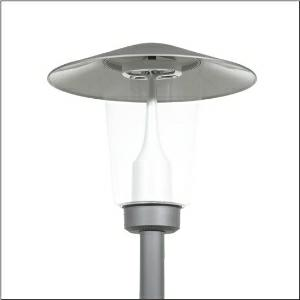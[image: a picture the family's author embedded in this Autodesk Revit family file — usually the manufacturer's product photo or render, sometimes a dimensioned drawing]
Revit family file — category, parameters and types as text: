
# Revit family: pilzleuchte_iq___st1_2a_5xa5235af14h_f6cb
name_source: partatom
category: Lighting Fixtures
units: mm (PartAtom-declared; Revit-internal decimal feet)

## family parameters
Cut with Voids When Loaded = No
Host = Face
Light Source = No
Part Type = Normal
Room Calculation Point = No
Round Connector Dimension = Use Diameter
Shared = No

## types (1)
- --- (1 x LED, 1550 lm, 12.9 W, 2200K)
    Apparent Load = 13 VA
    CIE Flux Codes = 24 61 93 98 100
    Color Rendering = 70
    Color Temperature = 2200K
    Default Elevation = 1800 mm
    Description = Mushroom Luminaire iQ, mast luminaire, Module 540 iQ-SR, primary light control with 3 zone facetted reflector, of plastic, silver coated, highly specular, structured, primary optical cover: cover, of PMMA, transparent, light distribution: ST1.2a, light emission: direct distribution, primary light characteristic: asymmetric, installation type: post-top, LED, High Power LED, rated luminous flux: 1.550lm, luminous efficacy: 120lm/W, light colour: 722, colour temperature: 2200K, control gear: iQ Street-Remote, control: pre-setting: logarithmic dimming characteristic, Street-Remote, Auto-Match, Temp-Guard, Lumen-Switch, Night-Set, Smart-Wire, Light-Fading, Desk-Remote (wireless, voltage-free reading and setting of iQ features in the workshop via application-optimized NFC function/RFID function), optimised constant luminous flux control (CLO 2.0), with terminal, 6-pole, max. 2.5mm², mains connection: 230..240V, AC, 50/60Hz, start of lifetime: 13W, end of service life: 13W, reduction: 6W, luminaire housing, upper part, of glass-fibre reinforced polyester, coated, Siteco® metallic grey (DB 702S), diameter: 650mm, height: 586mm, spigot size: d x l = 76 x 70mm (post-top) | with reducer (optional accessory) 60 x 70mm, mounting height: 3..5m, post-top mast mounting element, of diecast aluminium, coated, Siteco® metallic grey (DB 702S), Module 540 iQ-SR, traffic white (RAL 9016), equipment: standard, protection rating (complete): IP65, insulation class (complete): insulation class II (safety insulation), certification: CE, ENEC, VDE, packaging unit: 1 piece

Light Distribution: ST1.2a
    Height = 586 mm
    Lamp = 1 x LED
    Lamp Light Flux = 1550 lm
    Lamp Power = 12.9 W
    Lamp count = 1
    Length = 650 mm
    Luminous efficacy = 120 lm/W
    Manufacturer = Siteco
    ModVariant = No
    Model = 5XA5235AF14H
    Number of Poles = 1
    OnlyDefault = Yes
    Power Factor = 1
    Product Name = Pilzleuchte iQ | ST1.2a
    Product group = mast luminaire | pylon top
    ProductGroupID = 6100
    Protection Class = Protection class II
    Protection Degree = IP 65
    RLX_Detail_Level = 1
    RLX_Emergency_Light_Flux = 0 lm
    RLX_Emergency_Type = 0
    RLX_Emergency_Type_DB = No
    RlxData = <blob elided: 124257 chars, md5=b4fa3d6c>
    Socket = socket
    Standby Power = 0 W
    System Light Flux = 1550 lm
    System Power = 13 W
    Type Comments = factory setting: luminous flux: 100 % | dim-lin: 254 | 516 mA
    Type Image = l_1006077.jpg
    URL = http://relux.com
    VarID = @adj_160275
    Voltage = 0 V
    Weight = 0.00 kg
    Width = 0 mm  [stored 0 ft]

note: [stored X ft] marks values corroborated as IEEE doubles in the binary element streams (Revit-internal decimal feet)

## geometry (parser evidence)
native form markers: Blend x4, Sweep x10
no freeform markers — native parametric forms only
